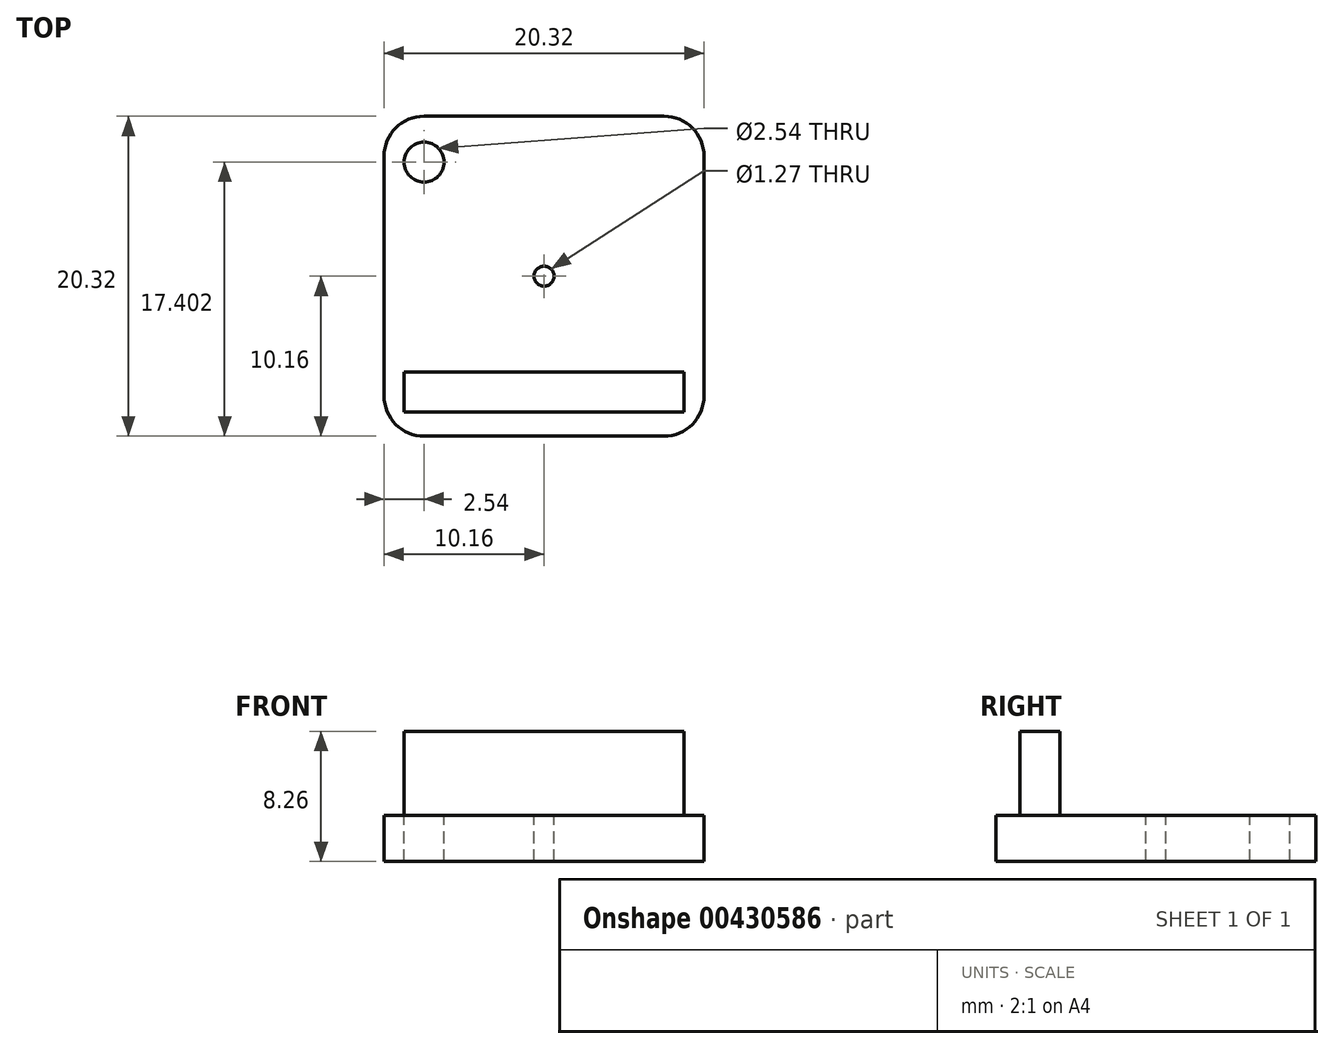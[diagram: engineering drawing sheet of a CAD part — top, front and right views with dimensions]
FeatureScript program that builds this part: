
annotation { "Feature Type Name" : "Feature", "Feature Type Description" : "" }
export const myFeature = defineFeature(function(context is Context, id is Id, definition is map)
    precondition{}
    {
        {
            var Q0;
            Q0=qCreatedBy(makeId("Top.planeOp"),FACE);
            var sketch = newSketch(context, id + "F0", { "sketchPlane" : qUnion([Q0])});
            skLineSegment(sketch, "E0.bottom", {"start": v(-10.16, 10.16) * mm, "end": v(10.16, 10.16) * mm});
            skLineSegment(sketch, "E0.top", {"start": v(-10.16, -10.16) * mm, "end": v(10.16, -10.16) * mm});
            skLineSegment(sketch, "E0.left", {"start": v(-10.16, 10.16) * mm, "end": v(-10.16, -10.16) * mm});
            skLineSegment(sketch, "E0.right", {"start": v(10.16, 10.16) * mm, "end": v(10.16, -10.16) * mm});
            skSolve(sketch);
        }
        {
            var Q0;
            Q0 = qSketchRegion(id + "F0", true);
            extrude(context, id + "F1", {"entities" : qUnion([Q0]), "depth" : 2.92 * mm});
        }
        {
            var Q0;
            Q0=makeQuery(id+"F1.opExtrude","CAP_FACE",FACE,{"disambiguationData":[OSD([sQuery(id+"F0.wireOp",EDGE,"E0.bottom"),sQuery(id+"F0.wireOp",EDGE,"E0.top"),sQuery(id+"F0.wireOp",EDGE,"E0.left"),sQuery(id+"F0.wireOp",EDGE,"E0.right")])],"isStart":false});
            var sketch = newSketch(context, id + "F2", { "sketchPlane" : qUnion([Q0])});
            skPoint(sketch, "E1", {"position": v(-7.62, 7.24) * mm});
            skSolve(sketch);
        }
        {
            var Q0;
            Q0=sQuery(id+"F2.wireOp",VERTEX,"E1");
            var Q1;
            Q1=makeQuery(id+"F1.opExtrude","SWEPT_BODY",BODY,{"disambiguationData":[OSD([sQuery(id+"F0.wireOp",EDGE,"E0.bottom"),sQuery(id+"F0.wireOp",EDGE,"E0.top"),sQuery(id+"F0.wireOp",EDGE,"E0.left"),sQuery(id+"F0.wireOp",EDGE,"E0.right")])]});
            hole(context, id + "F3", {"style" : HoleStyle.SIMPLE, "endStyle" : HoleEndStyle.THROUGH, "holeDiameter" : 2.54 * mm, "isTappedThrough" : true, "tappedDepth" : 12.7 * mm, "tapClearance" : 3, "locations" : qUnion([Q0]), "scope" : qUnion([Q1])});
        }
        {
            var Q0;
            Q0=makeQuery(id+"F1.opExtrude","CAP_FACE",FACE,{"disambiguationData":[OSD([sQuery(id+"F0.wireOp",EDGE,"E0.bottom"),sQuery(id+"F0.wireOp",EDGE,"E0.top"),sQuery(id+"F0.wireOp",EDGE,"E0.left"),sQuery(id+"F0.wireOp",EDGE,"E0.right")])],"isStart":false});
            var sketch = newSketch(context, id + "F4", { "sketchPlane" : qUnion([Q0])});
            skLineSegment(sketch, "E2.bottom", {"start": v(-8.89, -8.64) * mm, "end": v(8.89, -8.64) * mm});
            skLineSegment(sketch, "E2.top", {"start": v(-8.9, -6.1) * mm, "end": v(8.9, -6.1) * mm});
            skLineSegment(sketch, "E2.left", {"start": v(-8.9, -8.64) * mm, "end": v(-8.9, -6.1) * mm});
            skLineSegment(sketch, "E2.right", {"start": v(8.9, -8.64) * mm, "end": v(8.9, -6.1) * mm});
            skSolve(sketch);
        }
        {
            var Q0;
            Q0=makeQuery(id+"F1.opExtrude","SWEPT_EDGE",EDGE,{"disambiguationData":[OSD([sQuery(id+"F0.wireOp",EDGE,"E0.bottom"),sQuery(id+"F0.wireOp",EDGE,"E0.left")])]});
            var Q1;
            Q1=makeQuery(id+"F1.opExtrude","SWEPT_EDGE",EDGE,{"disambiguationData":[OSD([sQuery(id+"F0.wireOp",EDGE,"E0.bottom"),sQuery(id+"F0.wireOp",EDGE,"E0.right")])]});
            var Q2;
            Q2=makeQuery(id+"F1.opExtrude","SWEPT_EDGE",EDGE,{"disambiguationData":[OSD([sQuery(id+"F0.wireOp",EDGE,"E0.top"),sQuery(id+"F0.wireOp",EDGE,"E0.left")])]});
            var Q3;
            Q3=makeQuery(id+"F1.opExtrude","SWEPT_EDGE",EDGE,{"disambiguationData":[OSD([sQuery(id+"F0.wireOp",EDGE,"E0.top"),sQuery(id+"F0.wireOp",EDGE,"E0.right")])]});
            fillet(context, id + "F5", {"entities" : qUnion([Q0, Q1, Q2, Q3]), "radius" : 2.54 * mm, "tangentPropagation" : true, "allowEdgeOverflow" : false});
        }
        {
            var Q0;
            Q0 = qSketchRegion(id + "F4", true);
            extrude(context, id + "F6", {"entities" : qUnion([Q0]), "operationType" : NewBodyOperationType.ADD, "depth" : 5.33 * mm});
        }
        {
            var Q0;
            Q0=makeQuery(id+"F1.opExtrude","CAP_FACE",FACE,{"disambiguationData":[OSD([sQuery(id+"F0.wireOp",EDGE,"E0.bottom"),sQuery(id+"F0.wireOp",EDGE,"E0.top"),sQuery(id+"F0.wireOp",EDGE,"E0.left"),sQuery(id+"F0.wireOp",EDGE,"E0.right")])],"isStart":false});
            var sketch = newSketch(context, id + "F7", { "sketchPlane" : qUnion([Q0])});
            skPoint(sketch, "E3", {"position": v(0, 0) * mm});
            skSolve(sketch);
        }
        {
            var Q0;
            Q0=sQuery(id+"F7.wireOp",VERTEX,"E3");
            var Q1;
            Q1=makeQuery(id+"F1.opExtrude","SWEPT_BODY",BODY,{"disambiguationData":[OSD([sQuery(id+"F0.wireOp",EDGE,"E0.bottom"),sQuery(id+"F0.wireOp",EDGE,"E0.top"),sQuery(id+"F0.wireOp",EDGE,"E0.left"),sQuery(id+"F0.wireOp",EDGE,"E0.right")])]});
            hole(context, id + "F8", {"style" : HoleStyle.SIMPLE, "endStyle" : HoleEndStyle.THROUGH, "holeDiameter" : 1.27 * mm, "isTappedThrough" : true, "tappedDepth" : 12.7 * mm, "tapClearance" : 3, "startFromSketch" : true, "locations" : qUnion([Q0]), "scope" : qUnion([Q1])});
        }
    });
